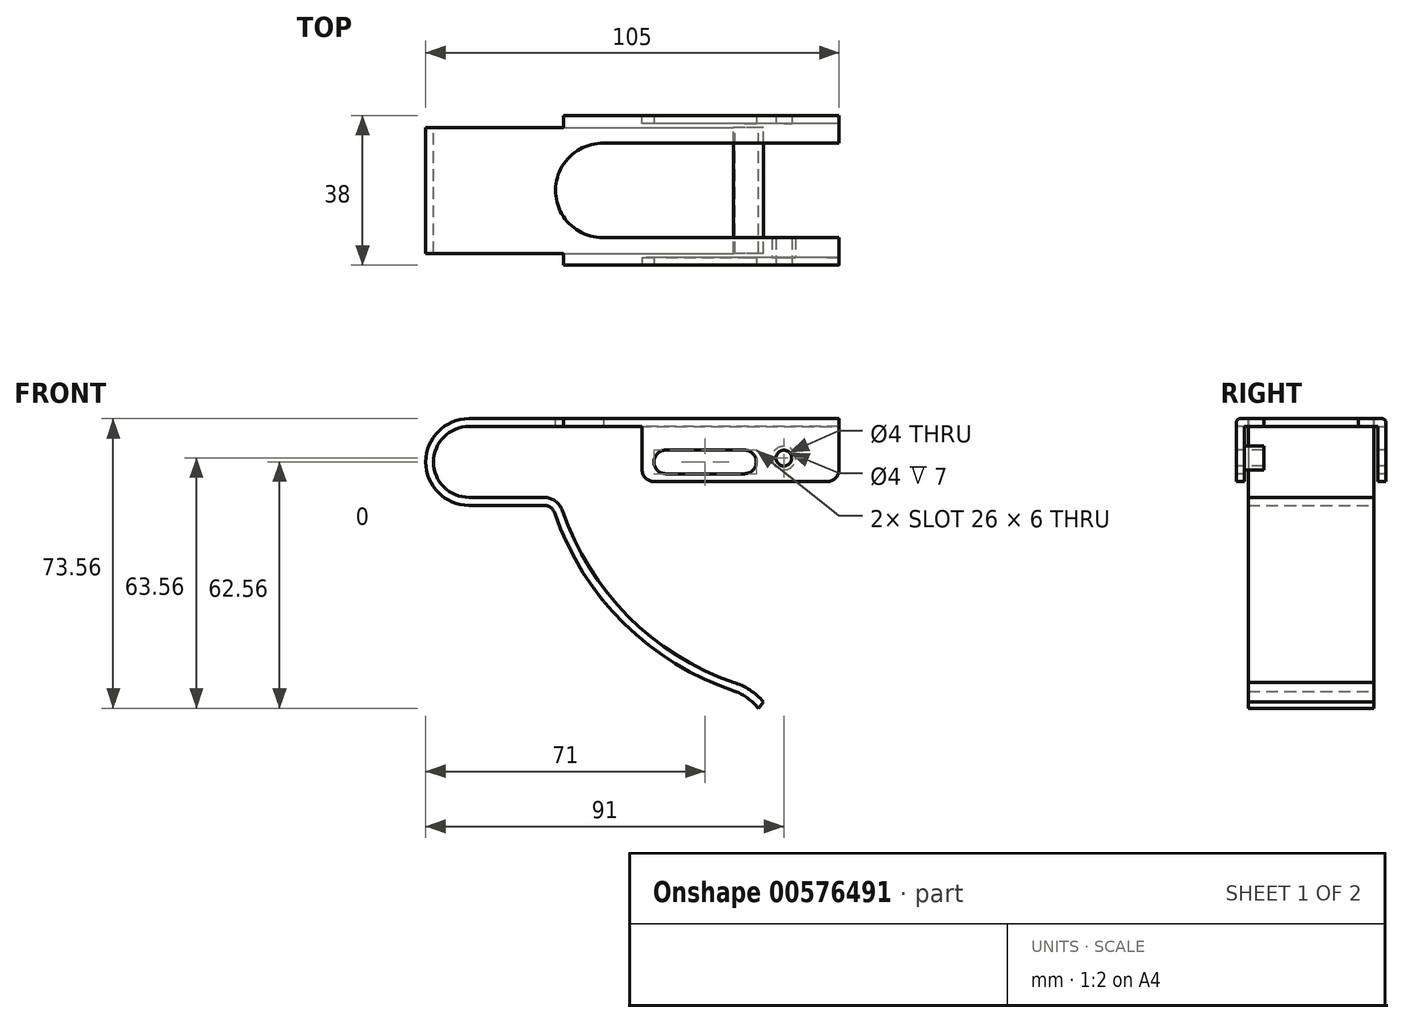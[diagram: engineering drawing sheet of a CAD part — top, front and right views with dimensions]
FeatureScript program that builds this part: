
annotation { "Feature Type Name" : "Feature", "Feature Type Description" : "" }
export const myFeature = defineFeature(function(context is Context, id is Id, definition is map)
    precondition{}
    {
        {
            var Q0;
            Q0=qCreatedBy(makeId("Front.planeOp"),FACE);
            var sketch = newSketch(context, id + "F0", { "sketchPlane" : qUnion([Q0])});
            skArc(sketch, "E0", {"start": v(0, 9) * mm, "mid": v(-9, 0) * mm, "end": v(0, -9) * mm});
            skLineSegment(sketch, "E1", {"start": v(0, 9) * mm, "end": v(94, 9) * mm});
            skLineSegment(sketch, "E2", {"start": v(0, -9) * mm, "end": v(19, -9) * mm});
            skArc(sketch, "E3", {"start": v(23.73, -12.39) * mm, "mid": v(40.4, -39.22) * mm, "end": v(67.15, -56) * mm});
            skPoint(sketch, "E4.visualSharp", {"position": v(22.67, -9) * mm});
            skArc(sketch, "E4.filletArc", {"start": v(23.73, -12.39) * mm, "mid": v(21.91, -9.93) * mm, "end": v(19, -9) * mm});
            skArc(sketch, "E5", {"start": v(74.8, -61) * mm, "mid": v(71.34, -57.94) * mm, "end": v(67.15, -56) * mm});
            skLineSegment(sketch, "E6.0", {"start": v(0, 11) * mm, "end": v(94, 11) * mm});
            skArc(sketch, "E6.1", {"start": v(0, 11) * mm, "mid": v(-11, 0) * mm, "end": v(0, -11) * mm});
            skArc(sketch, "E6.2", {"start": v(73.5, -62.56) * mm, "mid": v(70.82, -60) * mm, "end": v(67.57, -58.25) * mm});
            skArc(sketch, "E6.3", {"start": v(21.84, -13.03) * mm, "mid": v(39.38, -41.03) * mm, "end": v(67.57, -58.25) * mm});
            skArc(sketch, "E6.4", {"start": v(21.84, -13.03) * mm, "mid": v(20.75, -11.56) * mm, "end": v(19, -11) * mm});
            skLineSegment(sketch, "E6.5", {"start": v(0, -11) * mm, "end": v(19, -11) * mm});
            skLineSegment(sketch, "E7", {"start": v(94, 11) * mm, "end": v(94, 9) * mm});
            skLineSegment(sketch, "E8", {"start": v(74.8, -61) * mm, "end": v(73.5, -62.56) * mm});
            skLineSegment(sketch, "E9", {"start": v(74.8, -61) * mm, "end": v(90.94, -61) * mm, "construction": true});
            skSolve(sketch);
        }
        {
            var Q0;
            Q0 = qSketchRegion(id + "F0", true);
            extrude(context, id + "F1", {"entities" : qUnion([Q0]), "depth" : 16 * mm, "offsetDistance" : 25 * mm});
        }
        {
            var Q0;
            Q0=makeQuery(id+"F1.opExtrude","SWEPT_FACE",FACE,{"disambiguationData":[OSD([sQuery(id+"F0.wireOp",EDGE,"E6.0")])]});
            var sketch = newSketch(context, id + "F2", { "sketchPlane" : qUnion([Q0])});
            skLineSegment(sketch, "E10.bottom", {"start": v(94, -16) * mm, "end": v(24, -16) * mm});
            skLineSegment(sketch, "E10.top", {"start": v(94, -19) * mm, "end": v(24, -19) * mm});
            skLineSegment(sketch, "E10.left", {"start": v(94, -16) * mm, "end": v(94, -19) * mm});
            skLineSegment(sketch, "E10.right", {"start": v(24, -16) * mm, "end": v(24, -19) * mm});
            skSolve(sketch);
        }
        {
            var Q0;
            Q0 = qSketchRegion(id + "F2", true);
            extrude(context, id + "F3", {"entities" : qUnion([Q0]), "operationType" : NewBodyOperationType.ADD, "oppositeDirection" : true, "depth" : 2 * mm, "offsetDistance" : 25 * mm});
        }
        {
            var Q0;
            Q0=makeQuery(id+"F3.opExtrude","SWEPT_FACE",FACE,{"disambiguationData":[OSD([sQuery(id+"F2.wireOp",EDGE,"E10.top")])]});
            var sketch = newSketch(context, id + "F4", { "sketchPlane" : qUnion([Q0])});
            skLineSegment(sketch, "E11.bottom", {"start": v(94, 9) * mm, "end": v(44, 9) * mm});
            skLineSegment(sketch, "E11.top", {"start": v(94, -5) * mm, "end": v(44, -5) * mm});
            skLineSegment(sketch, "E11.left", {"start": v(94, 9) * mm, "end": v(94, -5) * mm});
            skLineSegment(sketch, "E11.right", {"start": v(44, 9) * mm, "end": v(44, -5) * mm});
            skSolve(sketch);
        }
        {
            var Q0;
            Q0 = qSketchRegion(id + "F4", true);
            extrude(context, id + "F5", {"entities" : qUnion([Q0]), "operationType" : NewBodyOperationType.ADD, "oppositeDirection" : true, "depth" : 2 * mm, "offsetDistance" : 25 * mm});
        }
        {
            var Q0;
            Q0=makeQuery(id+"F3.opExtrude","CAP_EDGE",EDGE,{"disambiguationData":[OSD([sQuery(id+"F2.wireOp",EDGE,"E10.top")])],"isStart":true});
            fillet(context, id + "F6", {"entities" : qUnion([Q0]), "radius" : 1 * mm, "allowEdgeOverflow" : false});
        }
        {
            var Q0;
            Q0=makeQuery(id+"F1.opExtrude","SWEPT_BODY",BODY,{"disambiguationData":[OSD([sQuery(id+"F0.wireOp",EDGE,"E0"),sQuery(id+"F0.wireOp",EDGE,"E1"),sQuery(id+"F0.wireOp",EDGE,"E2"),sQuery(id+"F0.wireOp",EDGE,"E3"),sQuery(id+"F0.wireOp",EDGE,"E4.filletArc"),sQuery(id+"F0.wireOp",EDGE,"E5"),sQuery(id+"F0.wireOp",EDGE,"E6.0"),sQuery(id+"F0.wireOp",EDGE,"E6.1"),sQuery(id+"F0.wireOp",EDGE,"E6.2"),sQuery(id+"F0.wireOp",EDGE,"E6.3"),sQuery(id+"F0.wireOp",EDGE,"E6.4"),sQuery(id+"F0.wireOp",EDGE,"E6.5"),sQuery(id+"F0.wireOp",EDGE,"E7"),sQuery(id+"F0.wireOp",EDGE,"E8")])]});
            var Q1;
            Q1=qCreatedBy(makeId("Front.planeOp"),FACE);
            mirror(context, id + "F7", {"operationType" : NewBodyOperationType.ADD, "entities" : qUnion([Q0]), "mirrorPlane" : qUnion([Q1])});
        }
        {
            var Q0;
            {var subQ0=makeQuery(id+"F3.boolean.opBoolean","MERGE",FACE,{"derivedFrom":[makeQuery(id+"F1.opExtrude","SWEPT_FACE",FACE,{"disambiguationData":[OSD([sQuery(id+"F0.wireOp",EDGE,"E6.0")])]}),makeQuery(id+"F3.opExtrude","CAP_FACE",FACE,{"disambiguationData":[OSD([sQuery(id+"F2.wireOp",EDGE,"E10.bottom"),sQuery(id+"F2.wireOp",EDGE,"E10.top"),sQuery(id+"F2.wireOp",EDGE,"E10.left"),sQuery(id+"F2.wireOp",EDGE,"E10.right")])],"isStart":true})]});Q0=makeQuery(id+"F7.boolean.opBoolean","MERGE",FACE,{"derivedFrom":[subQ0,makeQuery(id+"F7.opPattern","COPY",FACE,{"derivedFrom":subQ0,"instanceName":"1"})]});}
            var sketch = newSketch(context, id + "F8", { "sketchPlane" : qUnion([Q0])});
            skArc(sketch, "E12", {"start": v(34.27, 12) * mm, "mid": v(22, 0.14) * mm, "end": v(34, -12) * mm});
            skLineSegment(sketch, "E13", {"start": v(33.73, 12) * mm, "end": v(94, 12) * mm});
            skLineSegment(sketch, "E14", {"start": v(34, -12) * mm, "end": v(94, -12) * mm});
            skLineSegment(sketch, "E15", {"start": v(94, 12) * mm, "end": v(94, -12) * mm});
            skSolve(sketch);
        }
        {
            var Q0;
            Q0 = qSketchRegion(id + "F8", true);
            extrude(context, id + "F9", {"entities" : qUnion([Q0]), "operationType" : NewBodyOperationType.REMOVE, "oppositeDirection" : true, "depth" : 2 * mm, "offsetDistance" : 25 * mm});
        }
        {
            var Q0;
            Q0=makeQuery(id+"F5.boolean.opBoolean","MERGE",FACE,{"derivedFrom":[makeQuery(id+"F3.opExtrude","SWEPT_FACE",FACE,{"disambiguationData":[OSD([sQuery(id+"F2.wireOp",EDGE,"E10.top")])]}),makeQuery(id+"F5.opExtrude","CAP_FACE",FACE,{"disambiguationData":[OSD([sQuery(id+"F4.wireOp",EDGE,"E11.bottom"),sQuery(id+"F4.wireOp",EDGE,"E11.top"),sQuery(id+"F4.wireOp",EDGE,"E11.left"),sQuery(id+"F4.wireOp",EDGE,"E11.right")])],"isStart":true})]});
            var sketch = newSketch(context, id + "F10", { "sketchPlane" : qUnion([Q0])});
            skLineSegment(sketch, "E16", {"start": v(50, 0) * mm, "end": v(70, 0) * mm});
            skArc(sketch, "E17.0.startCap", {"start": v(50, -3) * mm, "mid": v(47, 0) * mm, "end": v(50, 3) * mm});
            skArc(sketch, "E17.0.endCap", {"start": v(70, 3) * mm, "mid": v(73, 0) * mm, "end": v(70, -3) * mm});
            skLineSegment(sketch, "E17.0.left", {"start": v(50, 3) * mm, "end": v(70, 3) * mm});
            skLineSegment(sketch, "E17.0.right", {"start": v(50, -3) * mm, "end": v(70, -3) * mm});
            skSolve(sketch);
        }
        {
            var Q0;
            Q0 = qSketchRegion(id + "F10", true);
            extrude(context, id + "F11", {"entities" : qUnion([Q0]), "operationType" : NewBodyOperationType.REMOVE, "endBound" : BoundingType.THROUGH_ALL, "oppositeDirection" : true, "depth" : 25 * mm, "offsetDistance" : 25 * mm});
        }
        {
            var Q0;
            Q0=makeQuery(id+"F5.boolean.opBoolean","MERGE",FACE,{"derivedFrom":[makeQuery(id+"F3.opExtrude","SWEPT_FACE",FACE,{"disambiguationData":[OSD([sQuery(id+"F2.wireOp",EDGE,"E10.top")])]}),makeQuery(id+"F5.opExtrude","CAP_FACE",FACE,{"disambiguationData":[OSD([sQuery(id+"F4.wireOp",EDGE,"E11.bottom"),sQuery(id+"F4.wireOp",EDGE,"E11.top"),sQuery(id+"F4.wireOp",EDGE,"E11.left"),sQuery(id+"F4.wireOp",EDGE,"E11.right")])],"isStart":true})]});
            var sketch = newSketch(context, id + "F12", { "sketchPlane" : qUnion([Q0])});
            skPoint(sketch, "E18", {"position": v(80, 1) * mm});
            skSolve(sketch);
        }
        {
            var Q0;
            Q0=sQuery(id+"F12.wireOp",VERTEX,"E18");
            var Q1;
            Q1=makeQuery(id+"F1.opExtrude","SWEPT_BODY",BODY,{"disambiguationData":[OSD([sQuery(id+"F0.wireOp",EDGE,"E0"),sQuery(id+"F0.wireOp",EDGE,"E1"),sQuery(id+"F0.wireOp",EDGE,"E2"),sQuery(id+"F0.wireOp",EDGE,"E3"),sQuery(id+"F0.wireOp",EDGE,"E4.filletArc"),sQuery(id+"F0.wireOp",EDGE,"E5"),sQuery(id+"F0.wireOp",EDGE,"E6.0"),sQuery(id+"F0.wireOp",EDGE,"E6.1"),sQuery(id+"F0.wireOp",EDGE,"E6.2"),sQuery(id+"F0.wireOp",EDGE,"E6.3"),sQuery(id+"F0.wireOp",EDGE,"E6.4"),sQuery(id+"F0.wireOp",EDGE,"E6.5"),sQuery(id+"F0.wireOp",EDGE,"E7"),sQuery(id+"F0.wireOp",EDGE,"E8")])]});
            hole(context, id + "F13", {"style" : HoleStyle.SIMPLE, "endStyle" : HoleEndStyle.THROUGH, "holeDiameter" : 4 * mm, "majorDiameter" : 5 * mm, "isTappedThrough" : true, "tappedDepth" : 12 * mm, "tapClearance" : 3, "locations" : qUnion([Q0]), "scope" : qUnion([Q1])});
        }
        {
            var Q0;
            Q0=makeQuery(id+"F5.opExtrude","CAP_FACE",FACE,{"disambiguationData":[OSD([sQuery(id+"F4.wireOp",EDGE,"E11.bottom"),sQuery(id+"F4.wireOp",EDGE,"E11.top"),sQuery(id+"F4.wireOp",EDGE,"E11.left"),sQuery(id+"F4.wireOp",EDGE,"E11.right")])],"isStart":false});
            var sketch = newSketch(context, id + "F14", { "sketchPlane" : qUnion([Q0])});
            skCircle(sketch, "E19.0", {"center": v(-80, 1) * mm, "radius": 2 * mm});
            skCircle(sketch, "E20.0", {"center": v(-80, 1) * mm, "radius": 3 * mm});
            skSolve(sketch);
        }
        {
            var Q0;
            Q0 = qSketchRegion(id + "F14", true);
            extrude(context, id + "F15", {"entities" : qUnion([Q0]), "operationType" : NewBodyOperationType.ADD, "depth" : 5 * mm, "offsetDistance" : 25 * mm});
        }
        {
            var Q0;
            Q0=makeQuery(id+"F5.opExtrude","SWEPT_EDGE",EDGE,{"disambiguationData":[OSD([sQuery(id+"F4.wireOp",EDGE,"E11.top"),sQuery(id+"F4.wireOp",EDGE,"E11.left")])]});
            var Q1;
            Q1=makeQuery(id+"F5.opExtrude","SWEPT_EDGE",EDGE,{"disambiguationData":[OSD([sQuery(id+"F4.wireOp",EDGE,"E11.top"),sQuery(id+"F4.wireOp",EDGE,"E11.right")])]});
            var Q2;
            Q2=makeQuery(id+"F7.opPattern","COPY",EDGE,{"derivedFrom":makeQuery(id+"F5.opExtrude","SWEPT_EDGE",EDGE,{"disambiguationData":[OSD([sQuery(id+"F4.wireOp",EDGE,"E11.top"),sQuery(id+"F4.wireOp",EDGE,"E11.left")])]}),"instanceName":"1"});
            var Q3;
            Q3=makeQuery(id+"F7.opPattern","COPY",EDGE,{"derivedFrom":makeQuery(id+"F5.opExtrude","SWEPT_EDGE",EDGE,{"disambiguationData":[OSD([sQuery(id+"F4.wireOp",EDGE,"E11.top"),sQuery(id+"F4.wireOp",EDGE,"E11.right")])]}),"instanceName":"1"});
            fillet(context, id + "F16", {"entities" : qUnion([Q0, Q1, Q2, Q3]), "radius" : 3 * mm, "tangentPropagation" : true, "allowEdgeOverflow" : false});
        }
    });
